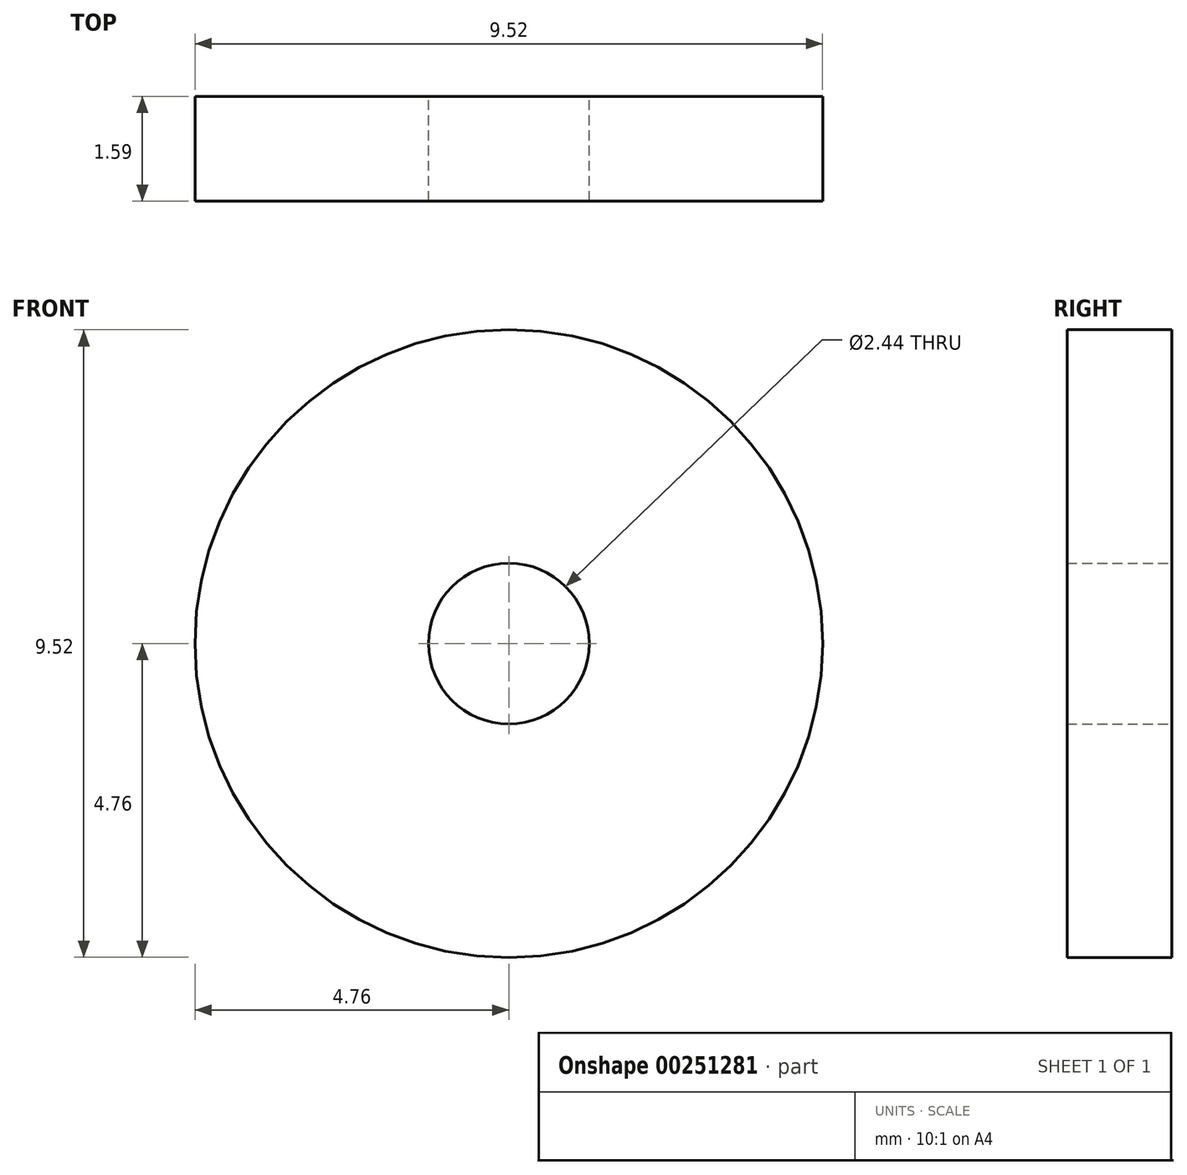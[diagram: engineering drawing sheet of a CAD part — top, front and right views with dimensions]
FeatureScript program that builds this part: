
annotation { "Feature Type Name" : "Feature", "Feature Type Description" : "" }
export const myFeature = defineFeature(function(context is Context, id is Id, definition is map)
    precondition{}
    {
        {
            var Q0;
            Q0=qCreatedBy(makeId("Front.planeOp"),FACE);
            var sketch = newSketch(context, id + "F0", { "sketchPlane" : qUnion([Q0])});
            skCircle(sketch, "E0", {"center": v(0, 0) * mm, "radius": 4.76 * mm});
            skCircle(sketch, "E1", {"center": v(0, 0) * mm, "radius": 1.22 * mm});
            skSolve(sketch);
        }
        {
            var Q0;
            Q0 = qSketchRegion(id + "F0", true);
            extrude(context, id + "F1", {"entities" : qUnion([Q0]), "depth" : 1.59 * mm});
        }
    });
